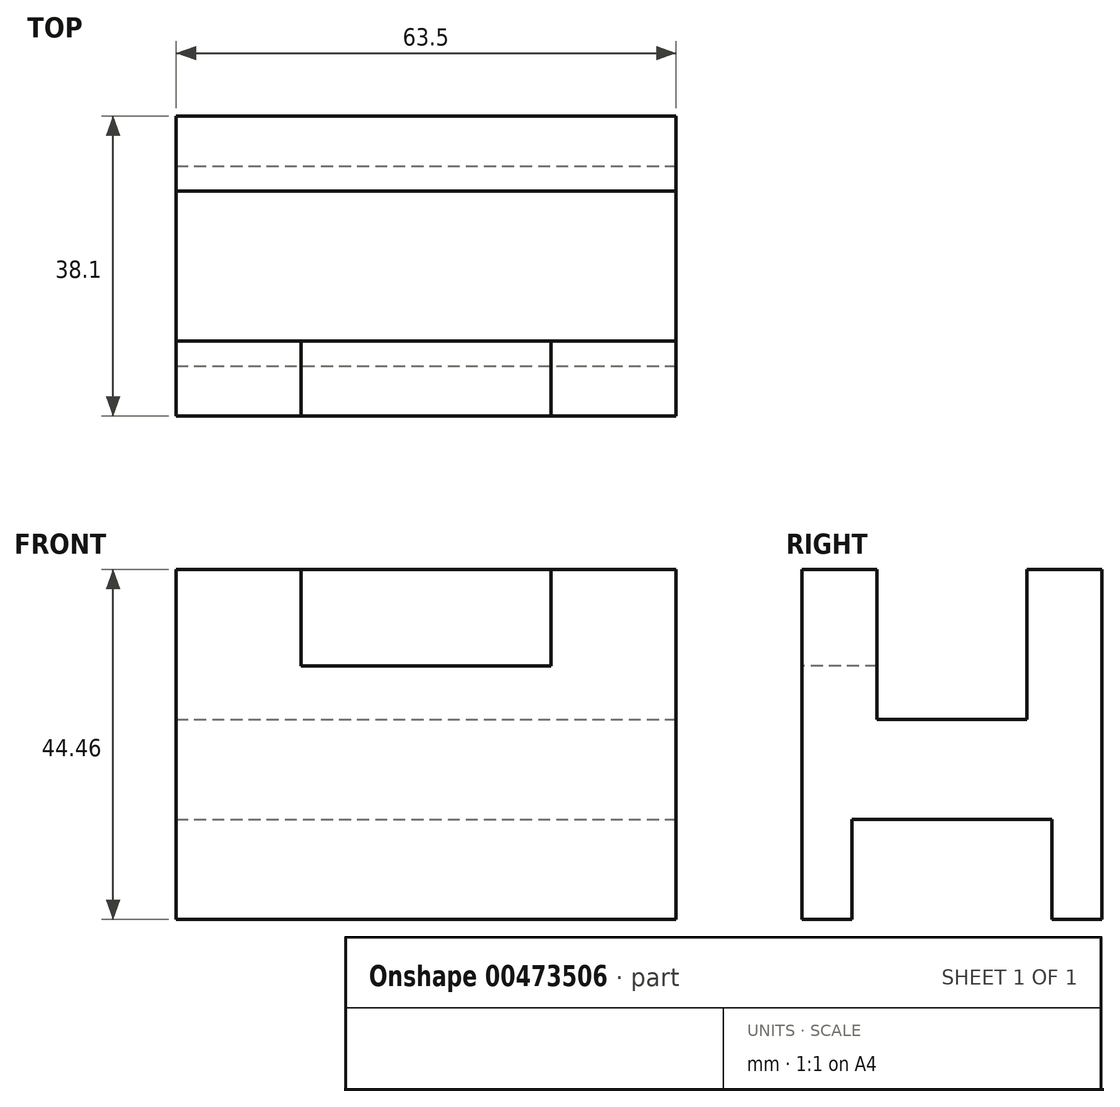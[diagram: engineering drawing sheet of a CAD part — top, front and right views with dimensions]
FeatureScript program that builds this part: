
annotation { "Feature Type Name" : "Feature", "Feature Type Description" : "" }
export const myFeature = defineFeature(function(context is Context, id is Id, definition is map)
    precondition{}
    {
        {
            var Q0;
            Q0=qCreatedBy(makeId("Front.planeOp"),FACE);
            var sketch = newSketch(context, id + "F0", { "sketchPlane" : qUnion([Q0])});
            skLineSegment(sketch, "E0.bottom", {"start": v(-31.75, 22.23) * mm, "end": v(31.75, 22.23) * mm});
            skLineSegment(sketch, "E0.top", {"start": v(-31.75, -22.23) * mm, "end": v(31.75, -22.23) * mm});
            skLineSegment(sketch, "E0.left", {"start": v(-31.75, 22.23) * mm, "end": v(-31.75, -22.23) * mm});
            skLineSegment(sketch, "E0.right", {"start": v(31.75, 22.23) * mm, "end": v(31.75, -22.23) * mm});
            skPoint(sketch, "E0.middle", {"position": v(0, 0) * mm});
            skSolve(sketch);
        }
        {
            var Q0;
            Q0 = qSketchRegion(id + "F0", true);
            extrude(context, id + "F1", {"entities" : qUnion([Q0]), "depth" : 38.1 * mm});
        }
        {
            var Q0;
            Q0=makeQuery(id+"F1.opExtrude","SWEPT_FACE",FACE,{"disambiguationData":[OSD([sQuery(id+"F0.wireOp",EDGE,"E0.right")])]});
            var sketch = newSketch(context, id + "F2", { "sketchPlane" : qUnion([Q0])});
            skLineSegment(sketch, "E1.bottom", {"start": v(-28.58, 22.23) * mm, "end": v(-9.53, 22.23) * mm});
            skLineSegment(sketch, "E1.top", {"start": v(-28.58, 3.18) * mm, "end": v(-9.53, 3.18) * mm});
            skLineSegment(sketch, "E1.left", {"start": v(-28.58, 22.23) * mm, "end": v(-28.58, 3.18) * mm});
            skLineSegment(sketch, "E1.right", {"start": v(-9.53, 22.23) * mm, "end": v(-9.53, 3.18) * mm});
            skSolve(sketch);
        }
        {
            var Q0;
            Q0 = qSketchRegion(id + "F2", true);
            extrude(context, id + "F3", {"entities" : qUnion([Q0]), "operationType" : NewBodyOperationType.REMOVE, "endBound" : BoundingType.THROUGH_ALL, "oppositeDirection" : true, "depth" : 25.4 * mm});
        }
        {
            var Q0;
            Q0=makeQuery(id+"F1.opExtrude","CAP_FACE",FACE,{"disambiguationData":[OSD([sQuery(id+"F0.wireOp",EDGE,"E0.bottom"),sQuery(id+"F0.wireOp",EDGE,"E0.top"),sQuery(id+"F0.wireOp",EDGE,"E0.left"),sQuery(id+"F0.wireOp",EDGE,"E0.right")])],"isStart":false});
            var sketch = newSketch(context, id + "F4", { "sketchPlane" : qUnion([Q0])});
            skLineSegment(sketch, "E2.bottom", {"start": v(-15.88, 22.23) * mm, "end": v(15.88, 22.23) * mm});
            skLineSegment(sketch, "E2.top", {"start": v(-15.88, 9.97) * mm, "end": v(15.88, 9.97) * mm});
            skLineSegment(sketch, "E2.left", {"start": v(-15.88, 22.23) * mm, "end": v(-15.88, 9.97) * mm});
            skLineSegment(sketch, "E2.right", {"start": v(15.88, 22.23) * mm, "end": v(15.88, 9.97) * mm});
            skSolve(sketch);
        }
        {
            var Q0;
            Q0 = qSketchRegion(id + "F4", true);
            extrude(context, id + "F5", {"entities" : qUnion([Q0]), "operationType" : NewBodyOperationType.REMOVE, "oppositeDirection" : true, "depth" : 9.52 * mm});
        }
        {
            var Q0;
            Q0=makeQuery(id+"F1.opExtrude","SWEPT_FACE",FACE,{"disambiguationData":[OSD([sQuery(id+"F0.wireOp",EDGE,"E0.right")])]});
            var sketch = newSketch(context, id + "F6", { "sketchPlane" : qUnion([Q0])});
            skLineSegment(sketch, "E3.bottom", {"start": v(-31.75, -22.23) * mm, "end": v(-6.35, -22.23) * mm});
            skLineSegment(sketch, "E3.top", {"start": v(-31.75, -9.52) * mm, "end": v(-6.35, -9.52) * mm});
            skLineSegment(sketch, "E3.left", {"start": v(-31.75, -22.23) * mm, "end": v(-31.75, -9.53) * mm});
            skLineSegment(sketch, "E3.right", {"start": v(-6.35, -22.23) * mm, "end": v(-6.35, -9.52) * mm});
            skSolve(sketch);
        }
        {
            var Q0;
            Q0 = qSketchRegion(id + "F6", true);
            extrude(context, id + "F7", {"entities" : qUnion([Q0]), "operationType" : NewBodyOperationType.REMOVE, "endBound" : BoundingType.THROUGH_ALL, "oppositeDirection" : true, "depth" : 25.4 * mm});
        }
    });
